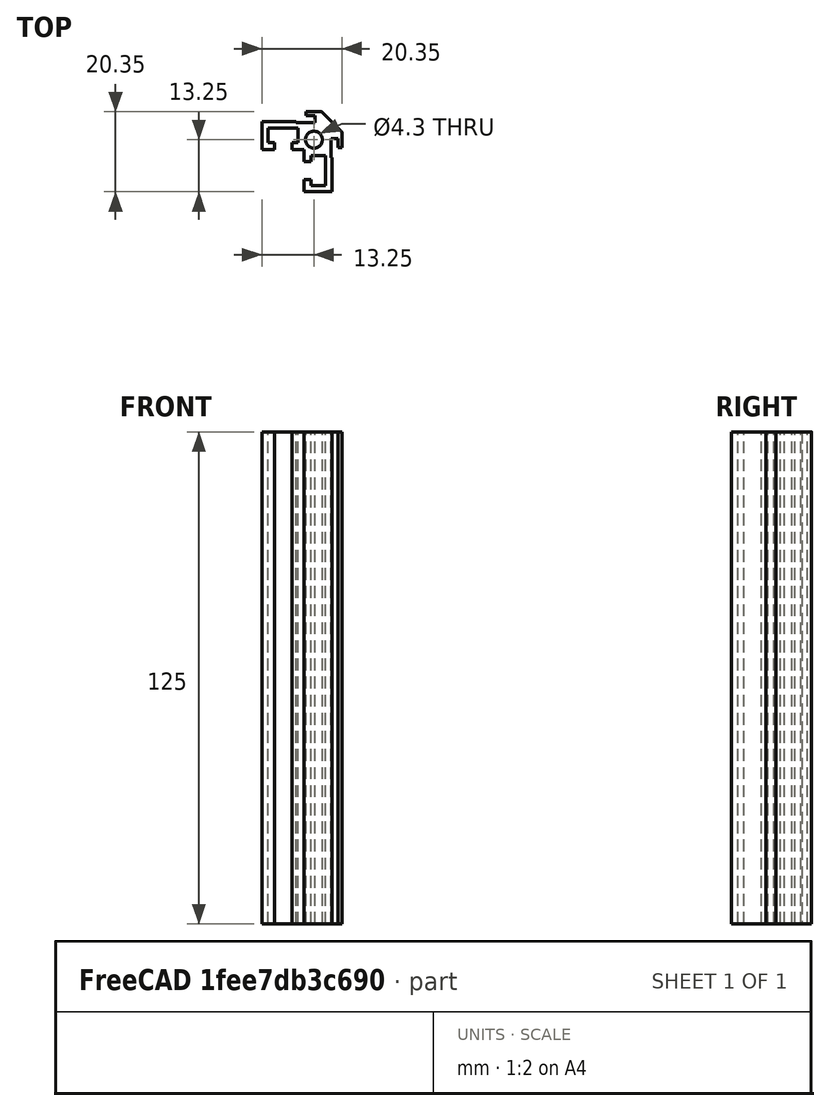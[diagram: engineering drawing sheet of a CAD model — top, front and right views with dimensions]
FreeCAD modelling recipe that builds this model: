
FCSTD DOCUMENT  (FreeCAD 0.18R16131 (Git))
Label: Frame
License: All rights reserved
LicenseURL: http://en.wikipedia.org/wiki/All_rights_reserved
objects: Part::Box×11, Part::Cut×11, Part::Cylinder×1, Part::Fillet×1, Part::Feature×1
note: 25 computed .brp shape members not serialized (recipe doc carries the construction recipe); baked Part::Feature solids carry a one-line shape summary decoded from their .brp

FEATURE [Part::Box] Box  label="Cube"
  AttacherType = Attacher::AttachEngine3D
  Height = 125
  Length = 20.35
  Width = 20.35
FEATURE [Part::Box] Box001  label="Cube001"
  AttacherType = Attacher::AttachEngine3D
  Height = 125
  Length = 10.75
  Width = 10.75
FEATURE [Part::Cut] Cut
  Base = -> Box
  Tool = -> Box001
FEATURE [Part::Box] Box002  label="Cube002"
  AttacherType = Attacher::AttachEngine3D
  Height = 125
  Length = 7.65
  Placement = pos=(1.6,12.5,0) rot=(0,0,1;0rad)
  Width = 3.65
FEATURE [Part::Box] Box003  label="Cube003"
  AttacherType = Attacher::AttachEngine3D
  Height = 125
  Length = 7.65
  Placement = pos=(12.5,9.25,0) rot=(0,0,-1;1.5708rad)
  Width = 3.65
FEATURE [Part::Box] Box004  label="Cube004"
  AttacherType = Attacher::AttachEngine3D
  Height = 125
  Length = 4.5
  Placement = pos=(3.2,10.75,0) rot=(0,0,1;0rad)
  Width = 1.75
FEATURE [Part::Cut] Cut001
  Base = -> Cut
  Tool = -> Box002
FEATURE [Part::Cut] Cut002
  Base = -> Cut001
  Tool = -> Box003
FEATURE [Part::Box] Box005  label="Cube005"
  AttacherType = Attacher::AttachEngine3D
  Height = 125
  Length = 4.5
  Placement = pos=(10.75,7.65,0) rot=(0,0,-1;1.5708rad)
  Width = 1.75
FEATURE [Part::Cut] Cut003
  Base = -> Cut002
  Tool = -> Box004
FEATURE [Part::Cut] Cut004
  Base = -> Cut003
  Tool = -> Box005
FEATURE [Part::Box] Box006  label="Cube006"
  AttacherType = Attacher::AttachEngine3D
  Height = 125
  Length = 11.25
  Placement = pos=(17.85,11.25,0) rot=(0,0,-1;1.5708rad)
  Width = 2.5
FEATURE [Part::Box] Box007  label="Cube007"
  AttacherType = Attacher::AttachEngine3D
  Height = 125
  Length = 11.25
  Placement = pos=(0,17.85,0) rot=(0,0,1;0rad)
  Width = 2.5
FEATURE [Part::Cut] Cut005
  Base = -> Cut004
  Tool = -> Box006
FEATURE [Part::Cut] Cut006
  Base = -> Cut005
  Tool = -> Box007
FEATURE [Part::Box] Box008  label="Cube008"
  AttacherType = Attacher::AttachEngine3D
  Height = 125
  Length = 8.75
  Placement = pos=(14.4,21.25,0) rot=(0,0,-1;0.785398rad)
  Width = 4.5
FEATURE [Part::Cut] Cut007
  Base = -> Cut006
  Tool = -> Box008
FEATURE [Part::Cylinder] Cylinder
  Angle = 360
  AttacherType = Attacher::AttachEngine3D
  Height = 125
  Placement = pos=(13.25,13.25,0) rot=(0,0,1;0rad)
  Radius = 2.15
FEATURE [Part::Cut] Cut008
  Base = -> Cut007
  Tool = -> Cylinder
FEATURE [Part::Box] Box009  label="Cube009"
  AttacherType = Attacher::AttachEngine3D
  Height = 125
  Length = 4.75
  Placement = pos=(17.6,13.5,0) rot=(0,0,-1;1.5708rad)
  Width = 1.75
FEATURE [Part::Box] Box010  label="Cube010"
  AttacherType = Attacher::AttachEngine3D
  Height = 125
  Length = 4.75
  Placement = pos=(8.75,17.6,0) rot=(0,0,1;0rad)
  Width = 1.75
FEATURE [Part::Cut] Cut009
  Base = -> Cut008
  Tool = -> Box009
FEATURE [Part::Cut] Cut010
  Base = -> Cut009
  Tool = -> Box010
FEATURE [Part::Fillet] Fillet  label="frame_source"
  Base = -> Cut010
  Edges = 2 edges r=1: [Edge82,Edge83]
FEATURE [Part::Feature] Fillet001  label="frame"
  shape: bbox 20.35 x 20.35 x 125 mm, 40 faces (baked)
